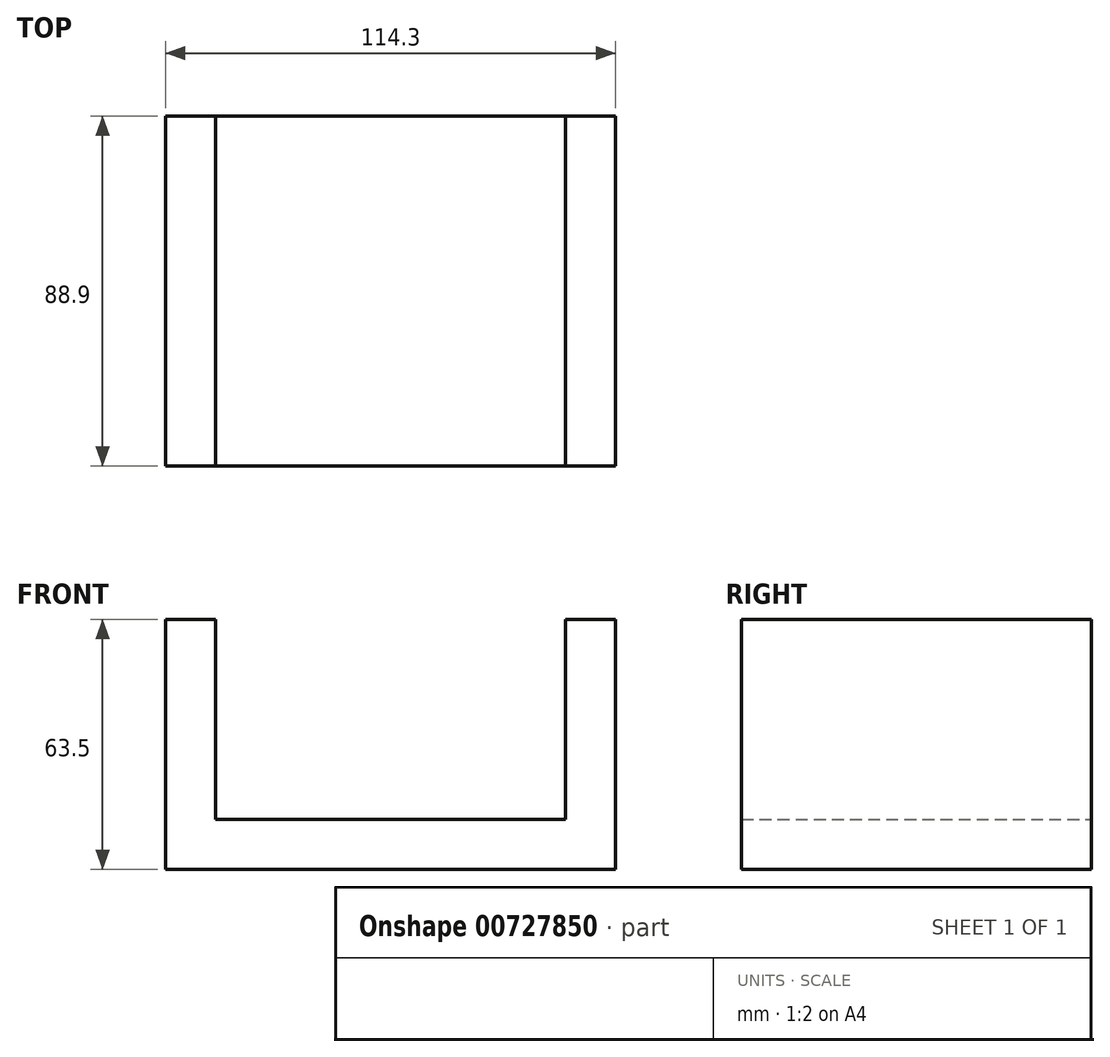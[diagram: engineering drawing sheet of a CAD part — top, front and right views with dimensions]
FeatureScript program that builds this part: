
annotation { "Feature Type Name" : "Feature", "Feature Type Description" : "" }
export const myFeature = defineFeature(function(context is Context, id is Id, definition is map)
    precondition{}
    {
        {
            var Q0;
            Q0=qCreatedBy(makeId("Front.planeOp"),FACE);
            var sketch = newSketch(context, id + "F0", { "sketchPlane" : qUnion([Q0])});
            skLineSegment(sketch, "E0", {"start": v(-73.2, 39.2) * mm, "end": v(-60.5, 39.2) * mm});
            skLineSegment(sketch, "E1", {"start": v(-60.5, 39.2) * mm, "end": v(-60.5, -11.6) * mm});
            skLineSegment(sketch, "E2", {"start": v(-60.5, -11.6) * mm, "end": v(28.4, -11.6) * mm});
            skLineSegment(sketch, "E3", {"start": v(28.4, -11.6) * mm, "end": v(28.4, 39.2) * mm});
            skLineSegment(sketch, "E4", {"start": v(28.4, 39.2) * mm, "end": v(41.1, 39.2) * mm});
            skLineSegment(sketch, "E5", {"start": v(41.1, 39.2) * mm, "end": v(41.1, -24.3) * mm});
            skLineSegment(sketch, "E6", {"start": v(41.1, -24.3) * mm, "end": v(-73.2, -24.3) * mm});
            skLineSegment(sketch, "E7", {"start": v(-73.2, -24.3) * mm, "end": v(-73.2, 39.2) * mm});
            skSolve(sketch);
        }
        {
            var Q0;
            Q0=makeQuery(id+"F0.imprint","IMPRINT",FACE,{"disambiguationData":[TD([[makeQuery(id+"F0.imprint","IMPRINT",EDGE,{"derivedFrom":sQuery(id+"F0.wireOp",EDGE,"E0")}),-1.0]])]});
            extrude(context, id + "F1", {"entities" : qUnion([Q0]), "depth" : 88.9 * mm, "offsetDistance" : 25.4 * mm});
        }
    });
